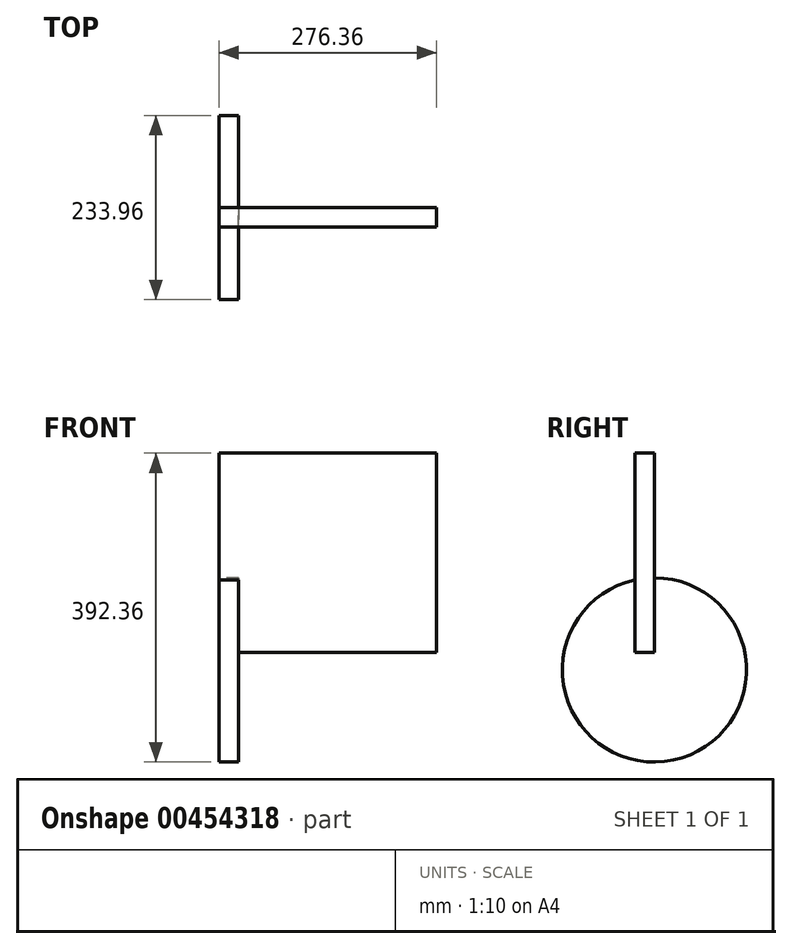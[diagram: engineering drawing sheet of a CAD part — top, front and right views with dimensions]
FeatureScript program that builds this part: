
annotation { "Feature Type Name" : "Feature", "Feature Type Description" : "" }
export const myFeature = defineFeature(function(context is Context, id is Id, definition is map)
    precondition{}
    {
        {
            var Q0;
            Q0=qCreatedBy(makeId("Right.planeOp"),FACE);
            var sketch = newSketch(context, id + "F0", { "sketchPlane" : qUnion([Q0])});
            skCircle(sketch, "E0", {"center": v(0, 0) * mm, "radius": 94.44 * mm});
            skSolve(sketch);
        }
        {
            var Q0;
            Q0=sQuery(id+"F0.wireOp",EDGE,"E0");
            extrude(context, id + "F1", {"bodyType" : ToolBodyType.SURFACE, "surfaceEntities" : qUnion([Q0]), "depth" : 26 * mm});
        }
        {
            var Q0;
            Q0=qCreatedBy(makeId("Right.planeOp"),FACE);
            var sketch = newSketch(context, id + "F2", { "sketchPlane" : qUnion([Q0])});
            skCircle(sketch, "E1", {"center": v(0, 0) * mm, "radius": 116.98 * mm});
            skSolve(sketch);
        }
        {
            var Q0;
            Q0 = qSketchRegion(id + "F2", true);
            extrude(context, id + "F3", {"entities" : qUnion([Q0]), "depth" : 25 * mm});
        }
        {
            var Q0;
            Q0=qCreatedBy(makeId("Front.planeOp"),FACE);
            var sketch = newSketch(context, id + "F4", { "sketchPlane" : qUnion([Q0])});
            skLineSegment(sketch, "E2.bottom", {"start": v(0, 22.5) * mm, "end": v(276.36, 22.5) * mm});
            skLineSegment(sketch, "E2.top", {"start": v(0, 275.38) * mm, "end": v(276.36, 275.38) * mm});
            skLineSegment(sketch, "E2.left", {"start": v(0, 22.5) * mm, "end": v(0, 275.38) * mm});
            skLineSegment(sketch, "E2.right", {"start": v(276.36, 22.5) * mm, "end": v(276.36, 275.38) * mm});
            skSolve(sketch);
        }
        {
            var Q0;
            Q0 = qSketchRegion(id + "F4", true);
            extrude(context, id + "F5", {"entities" : qUnion([Q0]), "operationType" : NewBodyOperationType.ADD, "depth" : 25 * mm});
        }
    });
